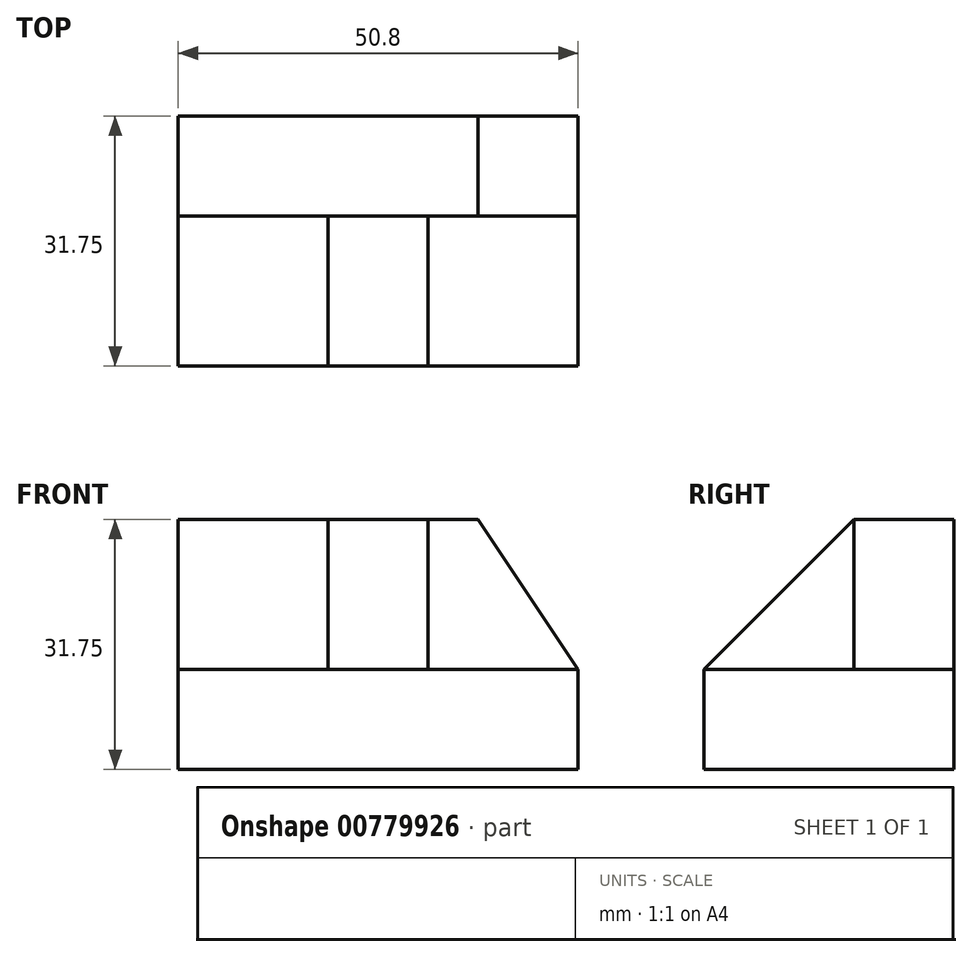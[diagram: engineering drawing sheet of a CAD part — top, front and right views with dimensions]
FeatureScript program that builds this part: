
annotation { "Feature Type Name" : "Feature", "Feature Type Description" : "" }
export const myFeature = defineFeature(function(context is Context, id is Id, definition is map)
    precondition{}
    {
        {
            var Q0;
            Q0=qCreatedBy(makeId("Front.planeOp"),FACE);
            var sketch = newSketch(context, id + "F0", { "sketchPlane" : qUnion([Q0])});
            skLineSegment(sketch, "E0", {"start": v(0, 0) * mm, "end": v(50.8, 0) * mm});
            skLineSegment(sketch, "E1", {"start": v(0, 31.75) * mm, "end": v(0, 0) * mm});
            skLineSegment(sketch, "E2", {"start": v(0, 31.75) * mm, "end": v(50.8, 31.75) * mm});
            skLineSegment(sketch, "E3", {"start": v(50.8, 31.75) * mm, "end": v(50.8, 0) * mm});
            skSolve(sketch);
        }
        {
            var Q0;
            Q0 = qSketchRegion(id + "F0", true);
            extrude(context, id + "F1", {"entities" : qUnion([Q0]), "depth" : 31.75 * mm, "offsetDistance" : 25.4 * mm});
        }
        {
            var Q0;
            Q0=makeQuery(id+"F1.opExtrude","SWEPT_FACE",FACE,{"disambiguationData":[OSD([sQuery(id+"F0.wireOp",EDGE,"E3")])]});
            var sketch = newSketch(context, id + "F2", { "sketchPlane" : qUnion([Q0])});
            skLineSegment(sketch, "E4", {"start": v(0, 31.75) * mm, "end": v(-12.7, 31.75) * mm});
            skLineSegment(sketch, "E5", {"start": v(-31.75, 0) * mm, "end": v(-31.75, 12.7) * mm});
            skLineSegment(sketch, "E6", {"start": v(-31.75, 12.7) * mm, "end": v(-12.7, 31.75) * mm});
            skSolve(sketch);
        }
        {
            var Q0;
            Q0=makeQuery(id+"F1.opExtrude","CAP_FACE",FACE,{"disambiguationData":[OSD([sQuery(id+"F0.wireOp",EDGE,"E0"),sQuery(id+"F0.wireOp",EDGE,"E1"),sQuery(id+"F0.wireOp",EDGE,"E2"),sQuery(id+"F0.wireOp",EDGE,"E3")])],"isStart":false});
            var sketch = newSketch(context, id + "F3", { "sketchPlane" : qUnion([Q0])});
            skLineSegment(sketch, "E7", {"start": v(0, 31.75) * mm, "end": v(19.05, 31.75) * mm});
            skLineSegment(sketch, "E8", {"start": v(19.05, 31.75) * mm, "end": v(19.05, 12.7) * mm});
            skLineSegment(sketch, "E9", {"start": v(19.05, 12.7) * mm, "end": v(31.75, 12.7) * mm});
            skLineSegment(sketch, "E10", {"start": v(31.75, 12.7) * mm, "end": v(31.75, 31.75) * mm});
            skLineSegment(sketch, "E11", {"start": v(19.05, 12.7) * mm, "end": v(0, 12.7) * mm});
            skLineSegment(sketch, "E12", {"start": v(31.75, 12.7) * mm, "end": v(50.8, 12.7) * mm});
            skSolve(sketch);
        }
        {
            var Q0;
            {var subQ0=sQuery(id+"F3.wireOp",EDGE,"E7");Q0=makeQuery(id+"F3.imprint","IMPRINT",FACE,{"disambiguationData":[TD([[makeQuery(id+"F3.imprint","IMPRINT",EDGE,{"derivedFrom":subQ0}),-1.0]])]});}
            var Q1;
            {var subQ0=sQuery(id+"F3.wireOp",EDGE,"E10");Q1=makeQuery(id+"F3.imprint","IMPRINT",FACE,{"disambiguationData":[TD([[makeQuery(id+"F3.imprint","IMPRINT",EDGE,{"derivedFrom":subQ0}),-1.0]])]});}
            extrude(context, id + "F4", {"entities" : qUnion([Q0, Q1]), "operationType" : NewBodyOperationType.REMOVE, "oppositeDirection" : true, "depth" : 19.05 * mm, "offsetDistance" : 25.4 * mm});
        }
        {
            var Q0;
            {var subQ0=sQuery(id+"F2.wireOp",EDGE,"E6");Q0=makeQuery(id+"F2.imprint","IMPRINT",FACE,{"disambiguationData":[TD([[makeQuery(id+"F2.imprint","IMPRINT",EDGE,{"derivedFrom":subQ0}),1.0]])]});}
            extrude(context, id + "F5", {"entities" : qUnion([Q0]), "operationType" : NewBodyOperationType.REMOVE, "oppositeDirection" : true, "depth" : 19.05 * mm, "offsetDistance" : 25.4 * mm});
        }
        {
            var Q0;
            Q0=makeQuery(id+"F4.boolean.opBoolean","COPY",FACE,{"derivedFrom":makeQuery(id+"F4.opExtrude","SWEPT_FACE",FACE,{"disambiguationData":[OSD([sQuery(id+"F3.wireOp",EDGE,"E10")])]})});
            var sketch = newSketch(context, id + "F6", { "sketchPlane" : qUnion([Q0])});
            skLineSegment(sketch, "E13", {"start": v(-12.7, 31.75) * mm, "end": v(-31.75, 12.7) * mm});
            skSolve(sketch);
        }
        {
            var Q0;
            Q0=makeQuery(id+"F6.imprint","IMPRINT",FACE,{"disambiguationData":[TD([[makeQuery(id+"F6.imprint","IMPRINT",EDGE,{"derivedFrom":sQuery(id+"F6.wireOp",EDGE,"E13")}),-1.0]])]});
            extrude(context, id + "F7", {"entities" : qUnion([Q0]), "operationType" : NewBodyOperationType.REMOVE, "oppositeDirection" : true, "depth" : 12.7 * mm, "offsetDistance" : 25.4 * mm});
        }
        {
            var Q0;
            Q0=makeQuery(id+"F4.boolean.opBoolean","COPY",FACE,{"derivedFrom":makeQuery(id+"F4.opExtrude","CAP_FACE",FACE,{"disambiguationData":[OSD([sQuery(id+"F0.wireOp",EDGE,"E2"),sQuery(id+"F0.wireOp",EDGE,"E3"),sQuery(id+"F3.wireOp",EDGE,"E10"),sQuery(id+"F3.wireOp",EDGE,"E12")])],"isStart":false})});
            var sketch = newSketch(context, id + "F8", { "sketchPlane" : qUnion([Q0])});
            skLineSegment(sketch, "E14", {"start": v(31.75, 31.75) * mm, "end": v(38.1, 31.75) * mm});
            skLineSegment(sketch, "E15", {"start": v(38.1, 31.75) * mm, "end": v(50.8, 12.7) * mm});
            skSolve(sketch);
        }
        {
            var Q0;
            {var subQ0=sQuery(id+"F8.wireOp",EDGE,"E15");Q0=makeQuery(id+"F8.imprint","IMPRINT",FACE,{"disambiguationData":[TD([[makeQuery(id+"F8.imprint","IMPRINT",EDGE,{"derivedFrom":subQ0}),1.0]])]});}
            extrude(context, id + "F9", {"entities" : qUnion([Q0]), "operationType" : NewBodyOperationType.REMOVE, "oppositeDirection" : true, "depth" : 12.7 * mm, "offsetDistance" : 25.4 * mm});
        }
    });
